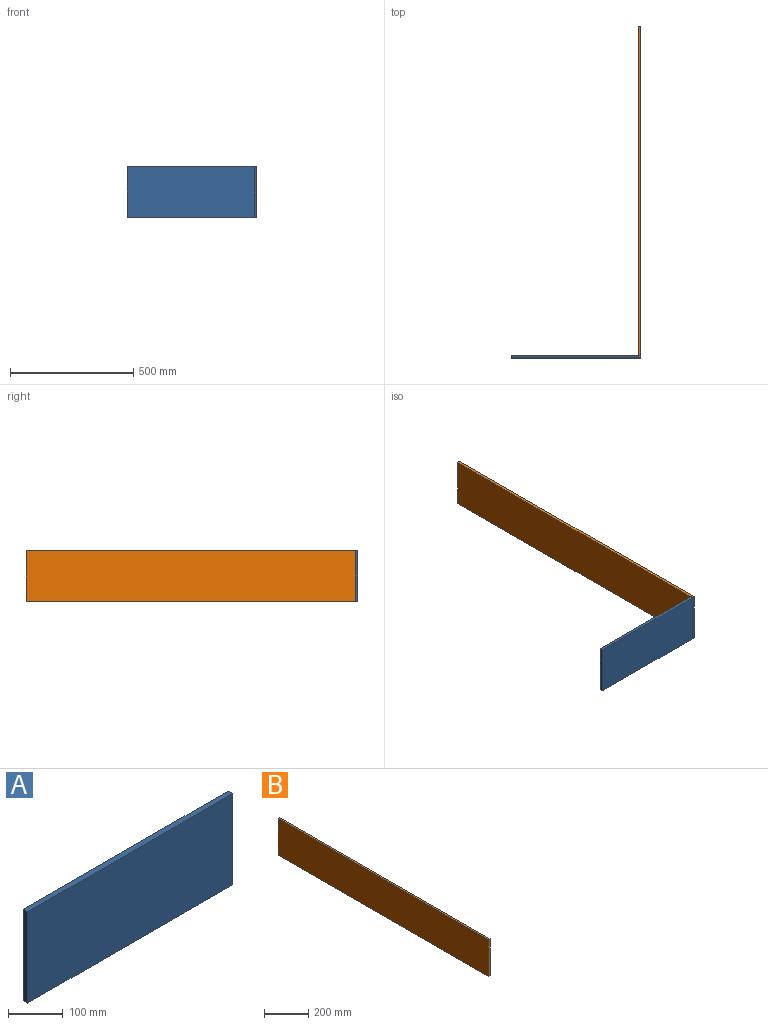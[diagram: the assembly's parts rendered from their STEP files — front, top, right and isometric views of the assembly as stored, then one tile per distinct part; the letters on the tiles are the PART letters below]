
ASSEMBLY  parts=2 mates=1
PART A: 6 faces, bbox 527.1x11.5x203.2 mm
  f0: plane 203.2x11.51mm, normal (-1,0,0), area 2338.1mm2, adj f1,f3,f4,f5
  f1: plane 527.05x11.51mm, normal (0,0,-1), area 6064.3mm2, adj f0,f2,f4,f5
  f2: plane 203.2x11.51mm, normal (1,0,0), area 2338.1mm2, adj f1,f3,f4,f5
  f3: plane 527.05x11.51mm, normal (0,0,1), area 6064.3mm2, adj f0,f2,f4,f5
  f4: plane 527.05x203.2mm, normal (0,-1,0), area 107096.6mm2, adj f0,f1,f2,f3
  f5: plane 527.05x203.2mm, normal (0,1,0), area 107096.6mm2, adj f0,f1,f2,f3
PART B: 6 faces, bbox 11.5x1346.2x203.2 mm
  f0: plane 203.2x11.51mm, normal (0,-1,0), area 2338.1mm2, adj f1,f3,f4,f5
  f1: plane 1346.2x11.51mm, normal (0,0,-1), area 15489.6mm2, adj f0,f2,f4,f5
  f2: plane 203.2x11.51mm, normal (0,1,0), area 2338.1mm2, adj f1,f3,f4,f5
  f3: plane 1346.2x11.51mm, normal (0,0,1), area 15489.6mm2, adj f0,f2,f4,f5
  f4: plane 1346.2x203.2mm, normal (1,0,0), area 273547.8mm2, adj f0,f1,f2,f3
  f5: plane 1346.2x203.2mm, normal (-1,0,0), area 273547.8mm2, adj f0,f1,f2,f3
PLACE A t=(82.67,-351.22,154.37)mm
PLACE B t=(348.2,271.34,176.89)mm
MATE fastened A.f2 <-> B.f4  axis (1,0,0) through (359.71,-362.73,159.03)mm
